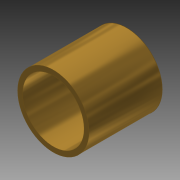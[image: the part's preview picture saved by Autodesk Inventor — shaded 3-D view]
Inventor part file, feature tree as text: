
AUTODESK INVENTOR PART (.ipt)
format: ipt  version: 2014 SP1 (Build 180222100, 222)  size: 88,064 bytes
history: native  units: in
note: dims shown in document units (in); Inventor stores cm internally (conversion verified against a paired STEP export)
features: extrude x1, sketch x1
ambient origin geometry x8: Origin, YZ Plane, XZ Plane, XY Plane, X Axis, Y Axis, Z Axis, Center Point
bodies: Solid1 (feature_tree)
feature tree (2):
  extrude  "Extrusion1"  Depth=0.45in
  sketch  "Sketch1"  dims[d0=0.379in d2=0.437in d3=0.45in d4=0.0in]
